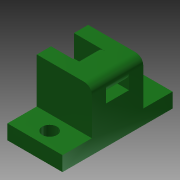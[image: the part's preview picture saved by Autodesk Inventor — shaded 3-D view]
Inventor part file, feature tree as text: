
AUTODESK INVENTOR PART (.ipt)
format: ipt  version: 2015 (Build 190159000, 159)  size: 162,816 bytes
history: native  units: mm
features: sketch x5, projected_geometry x5, extrude x4, fillet x2
ambient origin geometry x8: Origin, YZ Plane, XZ Plane, XY Plane, X Axis, Y Axis, Z Axis, Center Point
bodies: Solid1 (feature_tree)
feature tree (16):
  extrude  "Extrusion1"  Depth=15.0mm
  extrude  "Extrusion2"  Depth=22.0mm
  sketch  "Sketch3"  dims[d4=4.0mm d5=0.0mm d6=14.0mm d7=12.262mm d8=0.0mm]
  extrude  "Extrusion4"  Depth=14.0mm
  fillet  "Fillet1"  Radius=12.262mm
  extrude  "Extrusion5"  Depth=2.0mm
  fillet  "Fillet3"  Radius=1.11mm
  sketch  "Sketch1"  dims[d0=4.0mm d1=15.0mm]
  sketch  "Sketch2"  dims[d2=30.0mm d3=22.0mm]
  projected_geometry  "Projected Loop1"
  projected_geometry  "Projected Loop2"
  projected_geometry  "Projected Loop3"
  sketch  "Sketch4"  dims[d9=13.262mm d10=2.0mm d11=1.11mm]
  projected_geometry  "Projected Loop4"
  sketch  "Sketch5"  dims[d16=1.38mm d17=0.75mm d18=2.0mm d19=0.4mm d20=2.0mm d21=0.4mm d22=1.0mm d23=0.3mm d31=4.0mm d32=2.0mm d33=10.0mm d34=0.0mm d35=6.25mm d36=10.0mm d37=0.0mm d38=6.25mm]
  projected_geometry  "Projected Loop5"
